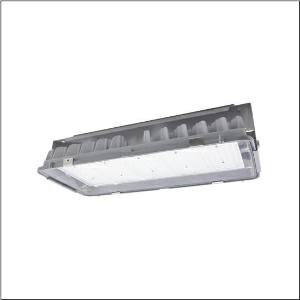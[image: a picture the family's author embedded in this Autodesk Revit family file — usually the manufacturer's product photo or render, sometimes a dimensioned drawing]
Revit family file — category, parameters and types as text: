
# Revit family: highbay_11xtreme_51hf62da4mma
name_source: partatom
category: Lighting Fixtures
units: mm (PartAtom-declared; Revit-internal decimal feet)

## family parameters
Cut with Voids When Loaded = No
Host = Face
Light Source = No
Part Type = Normal
Room Calculation Point = No
Round Connector Dimension = Use Diameter
Shared = No

## types (1)
- --- (1 x LED, 31100 lm, 170.9 W, 4000K)
    Apparent Load = 171 VA
    CIE Flux Codes = 84 96 100 100 100
    Color Rendering = 80
    Color Temperature = 4000K
    Default Elevation = 1800 mm
    Description = Highbay 11Xtreme, LED high bay luminaire, primary light control with lens, of PMMA, primary optical cover: cover, of toughened safety glass, light emission: direct distribution, primary light characteristic: symmetric, installation type: suspended mounting, surface-mounted, 1x LED module,for 1x LED, rated luminous flux: 31.100lm, luminous efficacy: 182lm/W, light colour: 840, colour temperature: 4000K, with cable H07RN-F 5x 1.5mm², mains connection: 220..240V, AC, 50/60Hz, cable length: 1,5m, rated input power: 171W, luminaire housing, of diecast aluminium, coated, silver, length: 595mm, width: 280mm, height: 195mm, protection rating (complete): IP66, insulation class (complete): insulation class I (protective earthing), certification: CE, ENEC, UKCA, protection symbol: D, ball protection: ball impact resistant according to DIN VDE 0710 part 13 (with chain suspension), impact resistance: IK08, permissible operating ambient temperature: -25..+60°C, reducing of maximum allowable ambient temperature of 5°C with ceiling mounting, packaging unit: 1 piece
    Height = 157 mm
    Lamp = 1 x LED
    Lamp Light Flux = 31100 lm
    Lamp Power = 170.9 W
    Lamp count = 1
    Length = 593 mm
    Luminous efficacy = 182 lm/W
    Manufacturer = Siteco
    ModVariant = No
    Model = 51HF62DA4MMA
    Mounting Place = Ceiling
    Mounting Type = Pendant
    Number of Poles = 1
    OnlyDefault = Yes
    Power Factor = 1
    Product Name = Highbay 11Xtreme
    Product group = LED high bay luminaire
    ProductGroupID = 903
    Protection Class = Protection class I
    Protection Degree = IP 66
    RLX_Detail_Level = 1
    RLX_Emergency_Light_Flux = 0 lm
    RLX_Emergency_Type = 0
    RLX_Emergency_Type_DB = No
    RlxData = <blob elided: 28341 chars, md5=55588596>
    Socket = socket
    Standby Power = 0 W
    System Light Flux = 31100 lm
    System Power = 171 W
    Type Comments = factory setting: luminous flux: 100 % | dim-lin: 254 | 1133 mA
    Type Image = l_1258342.jpg
    URL = http://relux.com
    VarID = @adj_035629
    Voltage = 0 V
    Weight = 0.00 kg
    Width = 568 mm

## geometry (parser evidence)
native form markers: Blend x4, Sweep x9
no freeform markers — native parametric forms only
